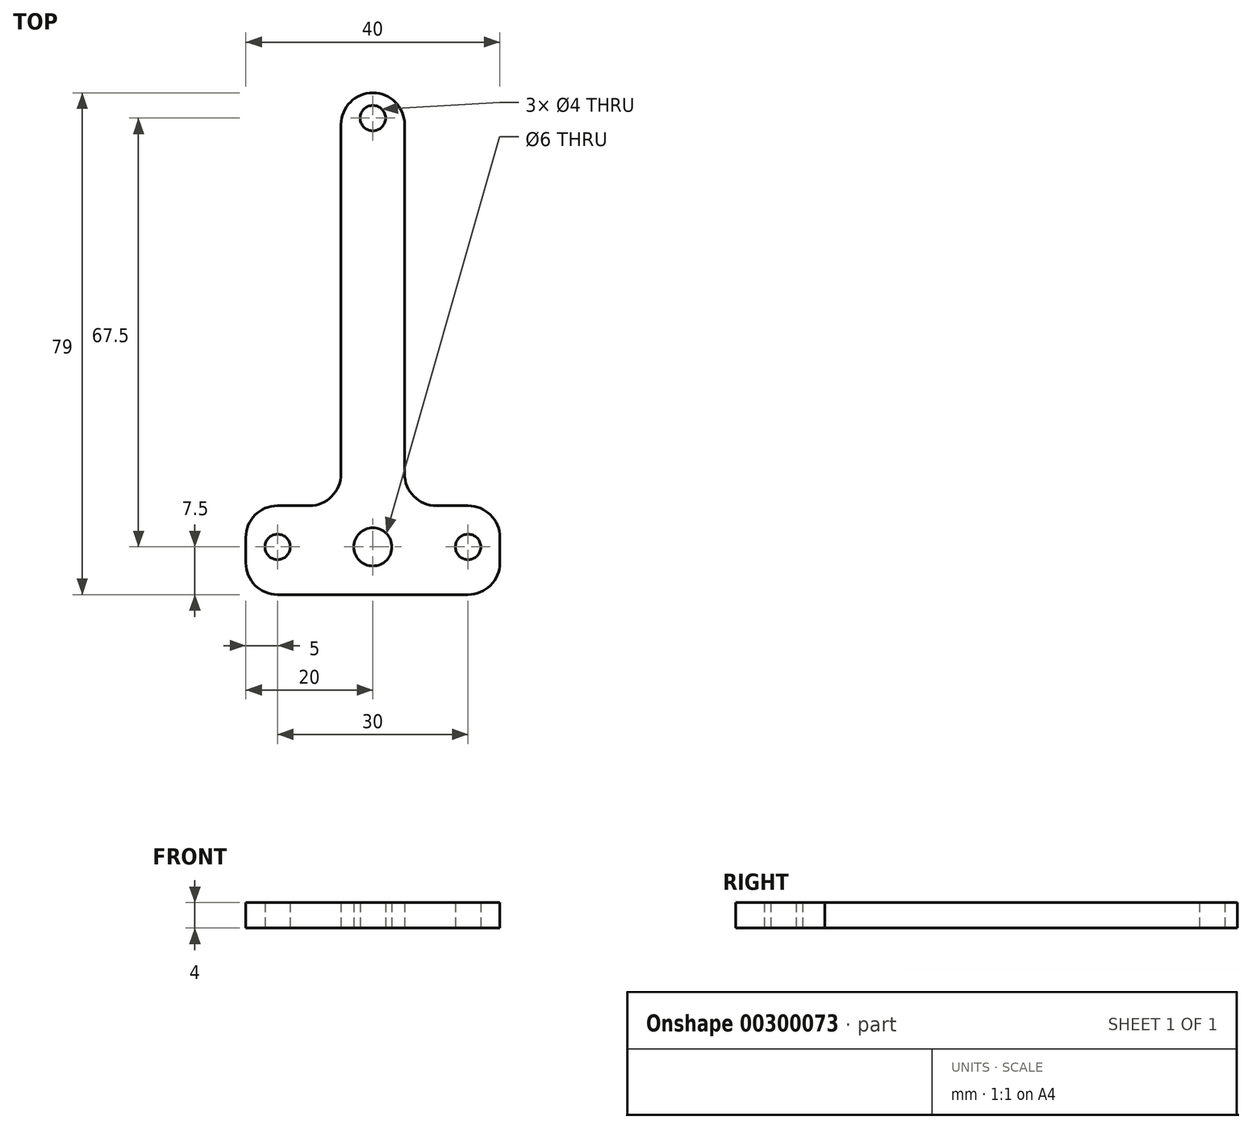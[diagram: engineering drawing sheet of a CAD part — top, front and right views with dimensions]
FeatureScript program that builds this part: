
annotation { "Feature Type Name" : "Feature", "Feature Type Description" : "" }
export const myFeature = defineFeature(function(context is Context, id is Id, definition is map)
    precondition{}
    {
        {
            var Q0;
            Q0=qCreatedBy(makeId("Top.planeOp"),FACE);
            var sketch = newSketch(context, id + "F0", { "sketchPlane" : qUnion([Q0])});
            skLineSegment(sketch, "E0", {"start": v(-20, 0) * mm, "end": v(20, 0) * mm});
            skLineSegment(sketch, "E1", {"start": v(20, 0) * mm, "end": v(20, 14) * mm});
            skLineSegment(sketch, "E2", {"start": v(20, 14) * mm, "end": v(5, 14) * mm});
            skLineSegment(sketch, "E3", {"start": v(5, 14) * mm, "end": v(5, 79) * mm});
            skLineSegment(sketch, "E4", {"start": v(5, 79) * mm, "end": v(-5, 79) * mm});
            skLineSegment(sketch, "E5", {"start": v(-5, 79) * mm, "end": v(-5, 14) * mm});
            skLineSegment(sketch, "E6", {"start": v(-20, 0) * mm, "end": v(-20, 14) * mm});
            skLineSegment(sketch, "E7", {"start": v(-20, 14) * mm, "end": v(-5, 14) * mm});
            skSolve(sketch);
        }
        {
            var Q0;
            Q0 = qSketchRegion(id + "F0", true);
            extrude(context, id + "F1", {"entities" : qUnion([Q0]), "depth" : 4 * mm});
        }
        {
            var Q0;
            Q0=qCreatedBy(makeId("Top.planeOp"),FACE);
            var sketch = newSketch(context, id + "F2", { "sketchPlane" : qUnion([Q0])});
            skCircle(sketch, "E8", {"center": v(-15, 7.5) * mm, "radius": 2 * mm});
            skCircle(sketch, "E9", {"center": v(15, 7.5) * mm, "radius": 2 * mm});
            skCircle(sketch, "E10", {"center": v(0, 75) * mm, "radius": 2 * mm});
            skCircle(sketch, "E11", {"center": v(0, 7.5) * mm, "radius": 3 * mm});
            skSolve(sketch);
        }
        {
            var Q0;
            Q0 = qSketchRegion(id + "F2", true);
            extrude(context, id + "F3", {"entities" : qUnion([Q0]), "operationType" : NewBodyOperationType.REMOVE, "depth" : 25 * mm});
        }
        {
            var Q0;
            Q0=makeQuery(id+"F1.opExtrude","SWEPT_EDGE",EDGE,{"disambiguationData":[OSD([sQuery(id+"F0.wireOp",EDGE,"E4"),sQuery(id+"F0.wireOp",EDGE,"E5")])]});
            var Q1;
            Q1=makeQuery(id+"F1.opExtrude","SWEPT_EDGE",EDGE,{"disambiguationData":[OSD([sQuery(id+"F0.wireOp",EDGE,"E3"),sQuery(id+"F0.wireOp",EDGE,"E4")])]});
            var Q2;
            Q2=makeQuery(id+"F1.opExtrude","SWEPT_EDGE",EDGE,{"disambiguationData":[OSD([sQuery(id+"F0.wireOp",EDGE,"E0"),sQuery(id+"F0.wireOp",EDGE,"E1")])]});
            var Q3;
            Q3=makeQuery(id+"F1.opExtrude","SWEPT_EDGE",EDGE,{"disambiguationData":[OSD([sQuery(id+"F0.wireOp",EDGE,"E0"),sQuery(id+"F0.wireOp",EDGE,"E6")])]});
            var Q4;
            Q4=makeQuery(id+"F1.opExtrude","SWEPT_EDGE",EDGE,{"disambiguationData":[OSD([sQuery(id+"F0.wireOp",EDGE,"E6"),sQuery(id+"F0.wireOp",EDGE,"E7")])]});
            var Q5;
            Q5=makeQuery(id+"F1.opExtrude","SWEPT_EDGE",EDGE,{"disambiguationData":[OSD([sQuery(id+"F0.wireOp",EDGE,"E1"),sQuery(id+"F0.wireOp",EDGE,"E2")])]});
            var Q6;
            Q6=makeQuery(id+"F1.opExtrude","SWEPT_EDGE",EDGE,{"disambiguationData":[OSD([sQuery(id+"F0.wireOp",EDGE,"E2"),sQuery(id+"F0.wireOp",EDGE,"E3")])]});
            var Q7;
            Q7=makeQuery(id+"F1.opExtrude","SWEPT_EDGE",EDGE,{"disambiguationData":[OSD([sQuery(id+"F0.wireOp",EDGE,"E5"),sQuery(id+"F0.wireOp",EDGE,"E7")])]});
            fillet(context, id + "F4", {"entities" : qUnion([Q0, Q1, Q2, Q3, Q4, Q5, Q6, Q7]), "radius" : 5 * mm, "tangentPropagation" : true, "allowEdgeOverflow" : false});
        }
    });
